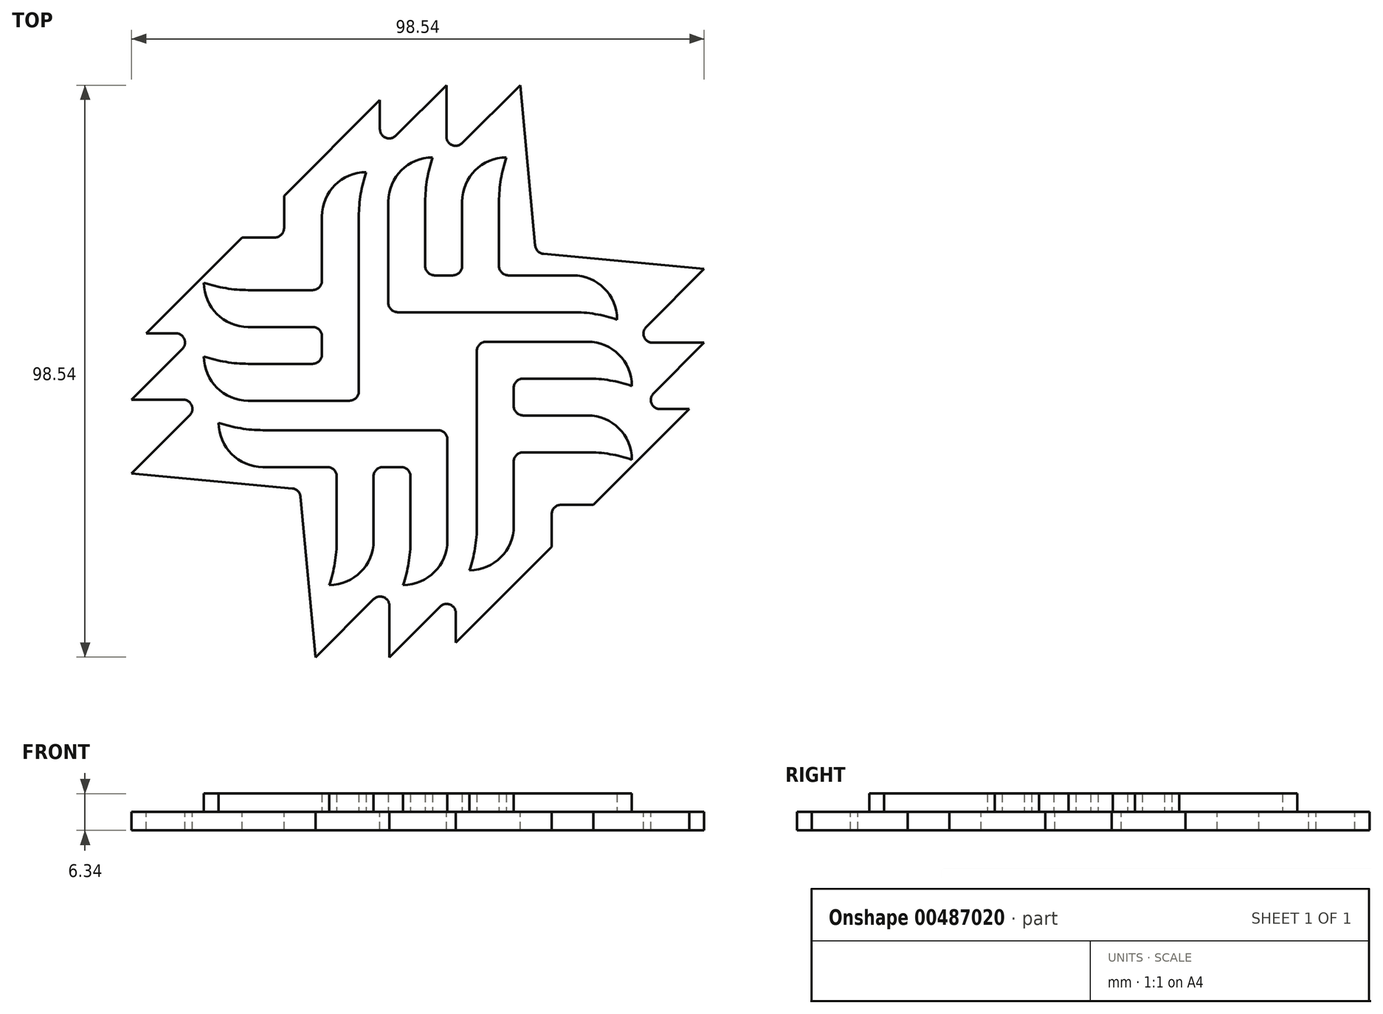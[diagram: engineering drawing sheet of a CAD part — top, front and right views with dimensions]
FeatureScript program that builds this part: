
annotation { "Feature Type Name" : "Feature", "Feature Type Description" : "" }
export const myFeature = defineFeature(function(context is Context, id is Id, definition is map)
    precondition{}
    {
        {
            var Q0;
            Q0=qCreatedBy(makeId("Top.planeOp"),FACE);
            var sketch = newSketch(context, id + "F0", { "sketchPlane" : qUnion([Q0])});
            skLineSegment(sketch, "E0", {"start": v(10.16, 3.5) * mm, "end": v(10.16, -26.67) * mm});
            skLineSegment(sketch, "E1", {"start": v(11.75, 5.08) * mm, "end": v(29.21, 5.08) * mm});
            skLineSegment(sketch, "E2", {"start": v(29.21, 5.08) * mm, "end": v(29.21, -1.27) * mm, "construction": true});
            skLineSegment(sketch, "E3", {"start": v(29.21, -1.27) * mm, "end": v(29.21, -2.54) * mm, "construction": true});
            skArc(sketch, "E4", {"start": v(29.21, 5.08) * mm, "mid": v(34.6, 2.85) * mm, "end": v(36.83, -2.54) * mm});
            skLineSegment(sketch, "E5", {"start": v(29.21, -1.27) * mm, "end": v(18.1, -1.27) * mm});
            skArc(sketch, "E6", {"start": v(36.83, -2.54) * mm, "mid": v(33.07, -1.59) * mm, "end": v(29.21, -1.27) * mm});
            skLineSegment(sketch, "E7", {"start": v(16.51, -2.86) * mm, "end": v(16.51, -6.03) * mm});
            skLineSegment(sketch, "E8", {"start": v(18.1, -7.62) * mm, "end": v(29.21, -7.62) * mm});
            skLineSegment(sketch, "E9", {"start": v(29.21, -7.62) * mm, "end": v(29.21, -13.97) * mm, "construction": true});
            skLineSegment(sketch, "E10", {"start": v(29.21, -13.97) * mm, "end": v(29.21, -15.24) * mm, "construction": true});
            skArc(sketch, "E11", {"start": v(29.21, -7.62) * mm, "mid": v(34.6, -9.85) * mm, "end": v(36.83, -15.24) * mm});
            skLineSegment(sketch, "E12", {"start": v(29.21, -13.97) * mm, "end": v(18.1, -13.97) * mm});
            skArc(sketch, "E13", {"start": v(36.83, -15.24) * mm, "mid": v(33.07, -14.29) * mm, "end": v(29.21, -13.97) * mm});
            skLineSegment(sketch, "E14", {"start": v(16.51, -15.56) * mm, "end": v(16.51, -26.67) * mm});
            skLineSegment(sketch, "E15", {"start": v(10.16, -26.67) * mm, "end": v(8.9, -26.67) * mm, "construction": true});
            skArc(sketch, "E16", {"start": v(16.51, -26.67) * mm, "mid": v(14.28, -32.06) * mm, "end": v(8.9, -34.3) * mm});
            skArc(sketch, "E17", {"start": v(8.9, -34.3) * mm, "mid": v(9.84, -30.53) * mm, "end": v(10.16, -26.67) * mm});
            skArc(sketch, "E18.filletArc", {"start": v(11.75, 5.08) * mm, "mid": v(10.62, 4.62) * mm, "end": v(10.16, 3.5) * mm});
            skPoint(sketch, "E19.visualSharp", {"position": v(16.51, -1.27) * mm});
            skArc(sketch, "E19.filletArc", {"start": v(18.1, -1.27) * mm, "mid": v(16.97, -1.73) * mm, "end": v(16.51, -2.86) * mm});
            skPoint(sketch, "E20.visualSharp", {"position": v(16.51, -7.62) * mm});
            skArc(sketch, "E20.filletArc", {"start": v(16.51, -6.03) * mm, "mid": v(16.97, -7.16) * mm, "end": v(18.1, -7.62) * mm});
            skPoint(sketch, "E21.visualSharp", {"position": v(16.51, -13.97) * mm});
            skArc(sketch, "E21.filletArc", {"start": v(18.1, -13.97) * mm, "mid": v(16.97, -14.43) * mm, "end": v(16.51, -15.56) * mm});
            skPoint(sketch, "E22", {"position": v(10.16, 5.08) * mm});
            skLineSegment(sketch, "E23", {"start": v(10.16, 5.08) * mm, "end": v(0, 5.08) * mm, "construction": true});
            skLineSegment(sketch, "E24", {"start": v(0, 5.08) * mm, "end": v(0, 0) * mm, "construction": true});
            skArc(sketch, "E25.1.0", {"start": v(34.3, 8.9) * mm, "mid": v(30.53, 9.84) * mm, "end": v(26.67, 10.16) * mm});
            skPoint(sketch, "E25.1.1", {"position": v(1.27, 16.51) * mm});
            skArc(sketch, "E25.1.2", {"start": v(26.67, 16.51) * mm, "mid": v(32.06, 14.28) * mm, "end": v(34.3, 8.9) * mm});
            skLineSegment(sketch, "E25.1.3", {"start": v(15.56, 16.51) * mm, "end": v(26.67, 16.51) * mm});
            skLineSegment(sketch, "E25.1.4", {"start": v(-3.5, 10.16) * mm, "end": v(26.67, 10.16) * mm});
            skArc(sketch, "E25.1.6", {"start": v(-5.08, 29.21) * mm, "mid": v(-2.85, 34.6) * mm, "end": v(2.54, 36.83) * mm});
            skArc(sketch, "E25.1.7", {"start": v(2.54, 36.83) * mm, "mid": v(1.59, 33.07) * mm, "end": v(1.27, 29.21) * mm});
            skLineSegment(sketch, "E25.1.8", {"start": v(7.62, 29.21) * mm, "end": v(13.97, 29.21) * mm, "construction": true});
            skPoint(sketch, "E25.1.9", {"position": v(7.62, 16.51) * mm});
            skPoint(sketch, "E25.1.10", {"position": v(-5.08, 10.16) * mm});
            skPoint(sketch, "E25.1.11", {"position": v(13.97, 16.51) * mm});
            skArc(sketch, "E25.1.13", {"start": v(15.24, 36.83) * mm, "mid": v(14.29, 33.07) * mm, "end": v(13.97, 29.21) * mm});
            skLineSegment(sketch, "E25.1.14", {"start": v(13.97, 29.21) * mm, "end": v(13.97, 18.1) * mm});
            skLineSegment(sketch, "E25.1.15", {"start": v(-5.08, 11.75) * mm, "end": v(-5.08, 29.21) * mm});
            skLineSegment(sketch, "E25.1.16", {"start": v(-5.08, 29.21) * mm, "end": v(1.27, 29.21) * mm, "construction": true});
            skArc(sketch, "E25.1.17", {"start": v(7.62, 29.21) * mm, "mid": v(9.85, 34.6) * mm, "end": v(15.24, 36.83) * mm});
            skLineSegment(sketch, "E25.1.18", {"start": v(1.27, 29.21) * mm, "end": v(1.27, 18.1) * mm});
            skLineSegment(sketch, "E25.1.19", {"start": v(2.86, 16.51) * mm, "end": v(6.03, 16.51) * mm});
            skLineSegment(sketch, "E25.1.20", {"start": v(7.62, 18.1) * mm, "end": v(7.62, 29.21) * mm});
            skArc(sketch, "E25.1.21", {"start": v(1.27, 18.1) * mm, "mid": v(1.73, 16.97) * mm, "end": v(2.86, 16.51) * mm});
            skArc(sketch, "E25.1.22", {"start": v(6.03, 16.51) * mm, "mid": v(7.16, 16.97) * mm, "end": v(7.62, 18.1) * mm});
            skArc(sketch, "E25.1.23", {"start": v(-5.08, 11.75) * mm, "mid": v(-4.62, 10.62) * mm, "end": v(-3.5, 10.16) * mm});
            skLineSegment(sketch, "E25.1.24", {"start": v(26.67, 10.16) * mm, "end": v(26.67, 8.9) * mm, "construction": true});
            skArc(sketch, "E25.1.25", {"start": v(13.97, 18.1) * mm, "mid": v(14.43, 16.97) * mm, "end": v(15.56, 16.51) * mm});
            skLineSegment(sketch, "E25.1.26", {"start": v(1.27, 29.21) * mm, "end": v(2.54, 29.21) * mm, "construction": true});
            skLineSegment(sketch, "E25.1.27", {"start": v(13.97, 29.21) * mm, "end": v(15.24, 29.21) * mm, "construction": true});
            skArc(sketch, "E25.2.0", {"start": v(-8.9, 34.3) * mm, "mid": v(-9.84, 30.53) * mm, "end": v(-10.16, 26.67) * mm});
            skPoint(sketch, "E25.2.1", {"position": v(-16.51, 1.27) * mm});
            skArc(sketch, "E25.2.2", {"start": v(-16.51, 26.67) * mm, "mid": v(-14.28, 32.06) * mm, "end": v(-8.9, 34.3) * mm});
            skLineSegment(sketch, "E25.2.3", {"start": v(-16.51, 15.56) * mm, "end": v(-16.51, 26.67) * mm});
            skLineSegment(sketch, "E25.2.4", {"start": v(-10.16, -3.5) * mm, "end": v(-10.16, 26.67) * mm});
            skArc(sketch, "E25.2.6", {"start": v(-29.21, -5.08) * mm, "mid": v(-34.6, -2.85) * mm, "end": v(-36.83, 2.54) * mm});
            skArc(sketch, "E25.2.7", {"start": v(-36.83, 2.54) * mm, "mid": v(-33.07, 1.59) * mm, "end": v(-29.21, 1.27) * mm});
            skLineSegment(sketch, "E25.2.8", {"start": v(-29.21, 7.62) * mm, "end": v(-29.21, 13.97) * mm, "construction": true});
            skPoint(sketch, "E25.2.9", {"position": v(-16.51, 7.62) * mm});
            skPoint(sketch, "E25.2.10", {"position": v(-10.16, -5.08) * mm});
            skPoint(sketch, "E25.2.11", {"position": v(-16.51, 13.97) * mm});
            skArc(sketch, "E25.2.13", {"start": v(-36.83, 15.24) * mm, "mid": v(-33.07, 14.29) * mm, "end": v(-29.21, 13.97) * mm});
            skLineSegment(sketch, "E25.2.14", {"start": v(-29.21, 13.97) * mm, "end": v(-18.1, 13.97) * mm});
            skLineSegment(sketch, "E25.2.15", {"start": v(-11.75, -5.08) * mm, "end": v(-29.21, -5.08) * mm});
            skLineSegment(sketch, "E25.2.16", {"start": v(-29.21, -5.08) * mm, "end": v(-29.21, 1.27) * mm, "construction": true});
            skArc(sketch, "E25.2.17", {"start": v(-29.21, 7.62) * mm, "mid": v(-34.6, 9.85) * mm, "end": v(-36.83, 15.24) * mm});
            skLineSegment(sketch, "E25.2.18", {"start": v(-29.21, 1.27) * mm, "end": v(-18.1, 1.27) * mm});
            skLineSegment(sketch, "E25.2.19", {"start": v(-16.51, 2.86) * mm, "end": v(-16.51, 6.03) * mm});
            skLineSegment(sketch, "E25.2.20", {"start": v(-18.1, 7.62) * mm, "end": v(-29.21, 7.62) * mm});
            skArc(sketch, "E25.2.21", {"start": v(-18.1, 1.27) * mm, "mid": v(-16.97, 1.73) * mm, "end": v(-16.51, 2.86) * mm});
            skArc(sketch, "E25.2.22", {"start": v(-16.51, 6.03) * mm, "mid": v(-16.97, 7.16) * mm, "end": v(-18.1, 7.62) * mm});
            skArc(sketch, "E25.2.23", {"start": v(-11.75, -5.08) * mm, "mid": v(-10.62, -4.62) * mm, "end": v(-10.16, -3.5) * mm});
            skLineSegment(sketch, "E25.2.24", {"start": v(-10.16, 26.67) * mm, "end": v(-8.9, 26.67) * mm, "construction": true});
            skArc(sketch, "E25.2.25", {"start": v(-18.1, 13.97) * mm, "mid": v(-16.97, 14.43) * mm, "end": v(-16.51, 15.56) * mm});
            skLineSegment(sketch, "E25.2.26", {"start": v(-29.21, 1.27) * mm, "end": v(-29.21, 2.54) * mm, "construction": true});
            skLineSegment(sketch, "E25.2.27", {"start": v(-29.21, 13.97) * mm, "end": v(-29.21, 15.24) * mm, "construction": true});
            skArc(sketch, "E25.3.0", {"start": v(-34.3, -8.9) * mm, "mid": v(-30.53, -9.84) * mm, "end": v(-26.67, -10.16) * mm});
            skPoint(sketch, "E25.3.1", {"position": v(-1.27, -16.51) * mm});
            skArc(sketch, "E25.3.2", {"start": v(-26.67, -16.51) * mm, "mid": v(-32.06, -14.28) * mm, "end": v(-34.3, -8.9) * mm});
            skLineSegment(sketch, "E25.3.3", {"start": v(-15.56, -16.51) * mm, "end": v(-26.67, -16.51) * mm});
            skLineSegment(sketch, "E25.3.4", {"start": v(3.5, -10.16) * mm, "end": v(-26.67, -10.16) * mm});
            skArc(sketch, "E25.3.6", {"start": v(5.08, -29.21) * mm, "mid": v(2.85, -34.6) * mm, "end": v(-2.54, -36.83) * mm});
            skArc(sketch, "E25.3.7", {"start": v(-2.54, -36.83) * mm, "mid": v(-1.59, -33.07) * mm, "end": v(-1.27, -29.21) * mm});
            skLineSegment(sketch, "E25.3.8", {"start": v(-7.62, -29.21) * mm, "end": v(-13.97, -29.21) * mm, "construction": true});
            skPoint(sketch, "E25.3.9", {"position": v(-7.62, -16.51) * mm});
            skPoint(sketch, "E25.3.10", {"position": v(5.08, -10.16) * mm});
            skPoint(sketch, "E25.3.11", {"position": v(-13.97, -16.51) * mm});
            skArc(sketch, "E25.3.13", {"start": v(-15.24, -36.83) * mm, "mid": v(-14.29, -33.07) * mm, "end": v(-13.97, -29.21) * mm});
            skLineSegment(sketch, "E25.3.14", {"start": v(-13.97, -29.21) * mm, "end": v(-13.97, -18.1) * mm});
            skLineSegment(sketch, "E25.3.15", {"start": v(5.08, -11.75) * mm, "end": v(5.08, -29.21) * mm});
            skLineSegment(sketch, "E25.3.16", {"start": v(5.08, -29.21) * mm, "end": v(-1.27, -29.21) * mm, "construction": true});
            skArc(sketch, "E25.3.17", {"start": v(-7.62, -29.21) * mm, "mid": v(-9.85, -34.6) * mm, "end": v(-15.24, -36.83) * mm});
            skLineSegment(sketch, "E25.3.18", {"start": v(-1.27, -29.21) * mm, "end": v(-1.27, -18.1) * mm});
            skLineSegment(sketch, "E25.3.19", {"start": v(-2.86, -16.51) * mm, "end": v(-6.03, -16.51) * mm});
            skLineSegment(sketch, "E25.3.20", {"start": v(-7.62, -18.1) * mm, "end": v(-7.62, -29.21) * mm});
            skArc(sketch, "E25.3.21", {"start": v(-1.27, -18.1) * mm, "mid": v(-1.73, -16.97) * mm, "end": v(-2.86, -16.51) * mm});
            skArc(sketch, "E25.3.22", {"start": v(-6.03, -16.51) * mm, "mid": v(-7.16, -16.97) * mm, "end": v(-7.62, -18.1) * mm});
            skArc(sketch, "E25.3.23", {"start": v(5.08, -11.75) * mm, "mid": v(4.62, -10.62) * mm, "end": v(3.5, -10.16) * mm});
            skLineSegment(sketch, "E25.3.24", {"start": v(-26.67, -10.16) * mm, "end": v(-26.67, -8.9) * mm, "construction": true});
            skArc(sketch, "E25.3.25", {"start": v(-13.97, -18.1) * mm, "mid": v(-14.43, -16.97) * mm, "end": v(-15.56, -16.51) * mm});
            skLineSegment(sketch, "E25.3.26", {"start": v(-1.27, -29.21) * mm, "end": v(-2.54, -29.21) * mm, "construction": true});
            skLineSegment(sketch, "E25.3.27", {"start": v(-13.97, -29.21) * mm, "end": v(-15.24, -29.21) * mm, "construction": true});
            skPoint(sketch, "E25.center", {"position": v(0, 0) * mm});
            skSolve(sketch);
        }
        {
            var Q0;
            Q0 = qSketchRegion(id + "F0", true);
            extrude(context, id + "F1", {"entities" : qUnion([Q0]), "depth" : 3.17 * mm, "offsetDistance" : 25.4 * mm});
        }
        {
            var Q0;
            Q0=qCreatedBy(makeId("Top.planeOp"),FACE);
            var sketch = newSketch(context, id + "F2", { "sketchPlane" : qUnion([Q0])});
            skPoint(sketch, "E26.0", {"position": v(10.16, 5.08) * mm});
            skPoint(sketch, "E26.1", {"position": v(16.51, -1.27) * mm});
            skPoint(sketch, "E26.2", {"position": v(16.51, -7.62) * mm});
            skPoint(sketch, "E26.3", {"position": v(16.51, -13.97) * mm});
            skLineSegment(sketch, "E27", {"start": v(10.16, 5.08) * mm, "end": v(29.21, 5.08) * mm, "construction": true});
            skLineSegment(sketch, "E28", {"start": v(29.21, 5.08) * mm, "end": v(29.21, -1.27) * mm, "construction": true});
            skLineSegment(sketch, "E29", {"start": v(29.21, -1.27) * mm, "end": v(35.56, -1.27) * mm, "construction": true});
            skLineSegment(sketch, "E30", {"start": v(35.56, -1.27) * mm, "end": v(29.21, 5.08) * mm, "construction": true});
            skLineSegment(sketch, "E31", {"start": v(35.56, -1.27) * mm, "end": v(16.51, -1.27) * mm, "construction": true});
            skLineSegment(sketch, "E32", {"start": v(16.51, -1.27) * mm, "end": v(16.51, -7.62) * mm, "construction": true});
            skLineSegment(sketch, "E33", {"start": v(16.51, -7.62) * mm, "end": v(29.21, -7.62) * mm, "construction": true});
            skLineSegment(sketch, "E34", {"start": v(29.21, -7.62) * mm, "end": v(29.21, -13.97) * mm, "construction": true});
            skLineSegment(sketch, "E35", {"start": v(29.21, -13.97) * mm, "end": v(35.56, -13.97) * mm, "construction": true});
            skLineSegment(sketch, "E36", {"start": v(35.56, -13.97) * mm, "end": v(29.21, -7.62) * mm, "construction": true});
            skLineSegment(sketch, "E37", {"start": v(35.56, -13.97) * mm, "end": v(16.51, -13.97) * mm, "construction": true});
            skLineSegment(sketch, "E38", {"start": v(16.51, -13.97) * mm, "end": v(16.51, -26.67) * mm, "construction": true});
            skLineSegment(sketch, "E39", {"start": v(16.51, -26.67) * mm, "end": v(10.16, -26.67) * mm, "construction": true});
            skLineSegment(sketch, "E40", {"start": v(10.16, -26.67) * mm, "end": v(10.16, -33.02) * mm, "construction": true});
            skLineSegment(sketch, "E41", {"start": v(16.51, -26.67) * mm, "end": v(10.16, -33.02) * mm, "construction": true});
            skLineSegment(sketch, "E42", {"start": v(10.16, -33.02) * mm, "end": v(10.16, 5.08) * mm, "construction": true});
            skLineSegment(sketch, "E43.5", {"start": v(6.53, -46.73) * mm, "end": v(6.53, -37.84) * mm});
            skLineSegment(sketch, "E43.6", {"start": v(23.04, -30.22) * mm, "end": v(6.53, -46.73) * mm});
            skLineSegment(sketch, "E43.7", {"start": v(23.04, -23.04) * mm, "end": v(23.04, -30.22) * mm});
            skLineSegment(sketch, "E44.3.2", {"start": v(-4.9, -49.27) * mm, "end": v(6.53, -37.84) * mm});
            skLineSegment(sketch, "E44.3.3", {"start": v(-4.9, -49.27) * mm, "end": v(-4.9, -36.57) * mm});
            skLineSegment(sketch, "E44.3.4", {"start": v(-17.6, -49.27) * mm, "end": v(-4.9, -36.57) * mm});
            skPoint(sketch, "E44.center", {"position": v(0, 0) * mm});
            skLineSegment(sketch, "E45.bottom", {"start": v(5.08, -5.08) * mm, "end": v(-5.08, -5.08) * mm, "construction": true});
            skLineSegment(sketch, "E45.top", {"start": v(5.08, 5.08) * mm, "end": v(-5.08, 5.08) * mm, "construction": true});
            skLineSegment(sketch, "E45.left", {"start": v(5.08, -5.08) * mm, "end": v(5.08, 5.08) * mm, "construction": true});
            skLineSegment(sketch, "E45.right", {"start": v(-5.08, -5.08) * mm, "end": v(-5.08, 5.08) * mm, "construction": true});
            skLineSegment(sketch, "E46", {"start": v(5.08, -5.08) * mm, "end": v(-5.08, 5.08) * mm, "construction": true});
            skLineSegment(sketch, "E47", {"start": v(-5.08, -5.08) * mm, "end": v(5.08, 5.08) * mm, "construction": true});
            skLineSegment(sketch, "E48.MirrorCS", {"start": v(49.27, 17.6) * mm, "end": v(36.57, 4.9) * mm});
            skLineSegment(sketch, "E49.MirrorCS", {"start": v(49.27, 4.9) * mm, "end": v(36.57, 4.9) * mm});
            skLineSegment(sketch, "E50.MirrorCS", {"start": v(49.27, 4.9) * mm, "end": v(37.84, -6.53) * mm});
            skLineSegment(sketch, "E51.MirrorCS", {"start": v(46.73, -6.53) * mm, "end": v(37.84, -6.53) * mm});
            skLineSegment(sketch, "E52.MirrorCS", {"start": v(23.04, -23.04) * mm, "end": v(30.22, -23.04) * mm});
            skLineSegment(sketch, "E53.MirrorCS", {"start": v(30.22, -23.04) * mm, "end": v(46.73, -6.53) * mm});
            skLineSegment(sketch, "E54", {"start": v(5.08, -5.08) * mm, "end": v(23.04, -23.04) * mm, "construction": true});
            skLineSegment(sketch, "E55.MirrorCS", {"start": v(17.6, 49.27) * mm, "end": v(4.9, 36.57) * mm});
            skLineSegment(sketch, "E56.MirrorCS", {"start": v(4.9, 49.27) * mm, "end": v(4.9, 36.57) * mm});
            skLineSegment(sketch, "E57.MirrorCS", {"start": v(4.9, 49.27) * mm, "end": v(-6.53, 37.84) * mm});
            skLineSegment(sketch, "E58.MirrorCS", {"start": v(-6.53, 46.73) * mm, "end": v(-6.53, 37.84) * mm});
            skLineSegment(sketch, "E59.MirrorCS", {"start": v(-23.04, 30.22) * mm, "end": v(-6.53, 46.73) * mm});
            skLineSegment(sketch, "E60.MirrorCS", {"start": v(-23.04, 23.04) * mm, "end": v(-23.04, 30.22) * mm});
            skLineSegment(sketch, "E61.MirrorCS", {"start": v(-23.04, 23.04) * mm, "end": v(-30.22, 23.04) * mm});
            skLineSegment(sketch, "E62.MirrorCS", {"start": v(-30.22, 23.04) * mm, "end": v(-46.73, 6.53) * mm});
            skLineSegment(sketch, "E63.MirrorCS", {"start": v(-46.73, 6.53) * mm, "end": v(-37.84, 6.53) * mm});
            skLineSegment(sketch, "E64.MirrorCS", {"start": v(-49.27, -4.9) * mm, "end": v(-37.84, 6.53) * mm});
            skLineSegment(sketch, "E65.MirrorCS", {"start": v(-49.27, -4.9) * mm, "end": v(-36.57, -4.9) * mm});
            skLineSegment(sketch, "E66.MirrorCS", {"start": v(-49.27, -17.6) * mm, "end": v(-36.57, -4.9) * mm});
            skPoint(sketch, "E67", {"position": v(-20.32, -20.32) * mm});
            skPoint(sketch, "E68", {"position": v(20.32, 20.32) * mm});
            skLineSegment(sketch, "E69", {"start": v(-49.27, -17.6) * mm, "end": v(-20.32, -20.32) * mm});
            skLineSegment(sketch, "E70", {"start": v(-17.6, -49.27) * mm, "end": v(-20.32, -20.32) * mm});
            skLineSegment(sketch, "E71", {"start": v(17.6, 49.27) * mm, "end": v(20.32, 20.32) * mm});
            skLineSegment(sketch, "E72", {"start": v(20.32, 20.32) * mm, "end": v(49.27, 17.6) * mm});
            skSolve(sketch);
        }
        {
            var Q0;
            Q0=makeQuery(id+"F2.imprint","IMPRINT",FACE,{"disambiguationData":[TD([[makeQuery(id+"F2.imprint","IMPRINT",EDGE,{"derivedFrom":sQuery(id+"F2.wireOp",EDGE,"E43.5")}),-1.0]])]});
            extrude(context, id + "F3", {"entities" : qUnion([Q0]), "oppositeDirection" : true, "depth" : 3.17 * mm, "offsetDistance" : 25.4 * mm});
        }
        {
            var Q0;
            Q0=makeQuery(id+"F3.opExtrude","SWEPT_EDGE",EDGE,{"disambiguationData":[OSD([sQuery(id+"F2.wireOp",EDGE,"E63.MirrorCS"),sQuery(id+"F2.wireOp",EDGE,"E64.MirrorCS")])]});
            var Q1;
            Q1=makeQuery(id+"F3.opExtrude","SWEPT_EDGE",EDGE,{"disambiguationData":[OSD([sQuery(id+"F2.wireOp",EDGE,"E65.MirrorCS"),sQuery(id+"F2.wireOp",EDGE,"E66.MirrorCS")])]});
            var Q2;
            Q2=makeQuery(id+"F3.opExtrude","SWEPT_EDGE",EDGE,{"disambiguationData":[OSD([sQuery(id+"F2.wireOp",EDGE,"E552.MirrorCS"),sQuery(id+"F2.wireOp",EDGE,"b8BfEYKk-opHP-SzIS-YWGw-rCtjwKep8GPD")])]});
            var Q3;
            Q3=makeQuery(id+"F3.opExtrude","SWEPT_EDGE",EDGE,{"disambiguationData":[OSD([sQuery(id+"F2.wireOp",EDGE,"E60.MirrorCS"),sQuery(id+"F2.wireOp",EDGE,"E61.MirrorCS")])]});
            var Q4;
            Q4=makeQuery(id+"F3.opExtrude","SWEPT_EDGE",EDGE,{"disambiguationData":[OSD([sQuery(id+"F2.wireOp",EDGE,"E57.MirrorCS"),sQuery(id+"F2.wireOp",EDGE,"E58.MirrorCS")])]});
            var Q5;
            Q5=makeQuery(id+"F3.opExtrude","SWEPT_EDGE",EDGE,{"disambiguationData":[OSD([sQuery(id+"F2.wireOp",EDGE,"E55.MirrorCS"),sQuery(id+"F2.wireOp",EDGE,"E56.MirrorCS")])]});
            var Q6;
            Q6=makeQuery(id+"F3.opExtrude","SWEPT_EDGE",EDGE,{"disambiguationData":[OSD([sQuery(id+"F2.wireOp",EDGE,"f88572ac-ed22-4b47-80f3-f8a6861cec2c0.MirrorCS"),sQuery(id+"F2.wireOp",EDGE,"SPc0mtcw-0f4n-yFXE-qiN2-ZiWwQtSucMF4")])]});
            var Q7;
            Q7=makeQuery(id+"F3.opExtrude","SWEPT_EDGE",EDGE,{"disambiguationData":[OSD([sQuery(id+"F2.wireOp",EDGE,"03fe7cb4-983f-44e6-97e3-664653cd00690.MirrorCS"),sQuery(id+"F2.wireOp",EDGE,"SPc0mtcw-0f4n-yFXE-qiN2-ZiWwQtSucMF4")])]});
            var Q8;
            Q8=makeQuery(id+"F3.opExtrude","SWEPT_EDGE",EDGE,{"disambiguationData":[OSD([sQuery(id+"F2.wireOp",EDGE,"E44.3.5"),sQuery(id+"F2.wireOp",EDGE,"b8BfEYKk-opHP-SzIS-YWGw-rCtjwKep8GPD")])]});
            var Q9;
            Q9=makeQuery(id+"F3.opExtrude","SWEPT_EDGE",EDGE,{"disambiguationData":[OSD([sQuery(id+"F2.wireOp",EDGE,"E44.3.3"),sQuery(id+"F2.wireOp",EDGE,"E44.3.4")])]});
            var Q10;
            Q10=makeQuery(id+"F3.opExtrude","SWEPT_EDGE",EDGE,{"disambiguationData":[OSD([sQuery(id+"F2.wireOp",EDGE,"E43.5"),sQuery(id+"F2.wireOp",EDGE,"E44.3.2")])]});
            var Q11;
            Q11=makeQuery(id+"F3.opExtrude","SWEPT_EDGE",EDGE,{"disambiguationData":[OSD([sQuery(id+"F2.wireOp",EDGE,"E43.7"),sQuery(id+"F2.wireOp",EDGE,"E52.MirrorCS")])]});
            var Q12;
            Q12=makeQuery(id+"F3.opExtrude","SWEPT_EDGE",EDGE,{"disambiguationData":[OSD([sQuery(id+"F2.wireOp",EDGE,"E50.MirrorCS"),sQuery(id+"F2.wireOp",EDGE,"E51.MirrorCS")])]});
            var Q13;
            Q13=makeQuery(id+"F3.opExtrude","SWEPT_EDGE",EDGE,{"disambiguationData":[OSD([sQuery(id+"F2.wireOp",EDGE,"E48.MirrorCS"),sQuery(id+"F2.wireOp",EDGE,"E49.MirrorCS")])]});
            var Q14;
            Q14=makeQuery(id+"F3.opExtrude","SWEPT_EDGE",EDGE,{"disambiguationData":[OSD([sQuery(id+"F2.wireOp",EDGE,"E71"),sQuery(id+"F2.wireOp",EDGE,"E72")])]});
            var Q15;
            Q15=makeQuery(id+"F3.opExtrude","SWEPT_EDGE",EDGE,{"disambiguationData":[OSD([sQuery(id+"F2.wireOp",EDGE,"E69"),sQuery(id+"F2.wireOp",EDGE,"E70")])]});
            fillet(context, id + "F4", {"entities" : qUnion([Q0, Q1, Q2, Q3, Q4, Q5, Q6, Q7, Q8, Q9, Q10, Q11, Q12, Q13, Q14, Q15]), "radius" : 1.59 * mm, "tangentPropagation" : true, "allowEdgeOverflow" : false});
        }
    });
